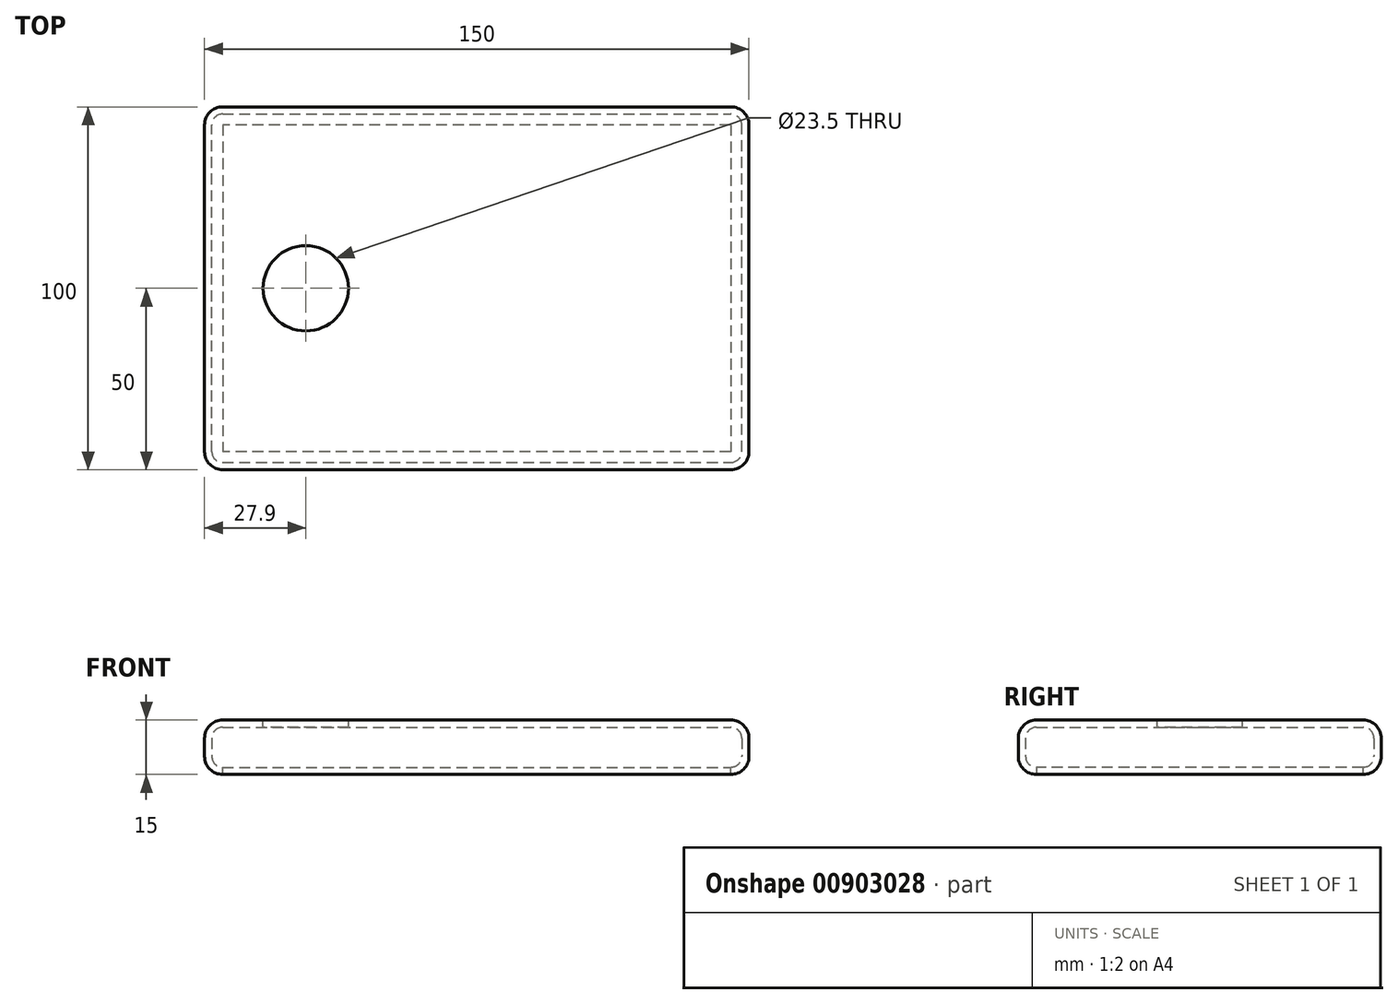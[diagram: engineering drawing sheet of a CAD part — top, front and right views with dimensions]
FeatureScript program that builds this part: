
annotation { "Feature Type Name" : "Feature", "Feature Type Description" : "" }
export const myFeature = defineFeature(function(context is Context, id is Id, definition is map)
    precondition{}
    {
        {
            var Q0;
            Q0=qCreatedBy(makeId("Top.planeOp"),FACE);
            var sketch = newSketch(context, id + "F0", { "sketchPlane" : qUnion([Q0])});
            skLineSegment(sketch, "E0.bottom", {"start": v(75, 50) * mm, "end": v(-75, 50) * mm});
            skLineSegment(sketch, "E0.top", {"start": v(75, -50) * mm, "end": v(-75, -50) * mm});
            skLineSegment(sketch, "E0.left", {"start": v(75, 50) * mm, "end": v(75, -50) * mm});
            skLineSegment(sketch, "E0.right", {"start": v(-75, 50) * mm, "end": v(-75, -50) * mm});
            skPoint(sketch, "E0.middle", {"position": v(0, 0) * mm});
            skSolve(sketch);
        }
        {
            var Q0;
            Q0=makeQuery(id+"F0.imprint","IMPRINT",FACE,{"disambiguationData":[TD([[makeQuery(id+"F0.imprint","IMPRINT",EDGE,{"derivedFrom":sQuery(id+"F0.wireOp",EDGE,"E0.bottom")}),1.0]])]});
            extrude(context, id + "F1", {"entities" : qUnion([Q0]), "depth" : 15 * mm, "offsetDistance" : 25 * mm});
        }
        {
            var Q0;
            Q0=makeQuery(id+"F1.opExtrude","CAP_EDGE",EDGE,{"disambiguationData":[OSD([sQuery(id+"F0.wireOp",EDGE,"E0.bottom")])],"isStart":true});
            var Q1;
            Q1=makeQuery(id+"F1.opExtrude","CAP_FACE",FACE,{"disambiguationData":[OSD([sQuery(id+"F0.wireOp",EDGE,"E0.bottom"),sQuery(id+"F0.wireOp",EDGE,"E0.top"),sQuery(id+"F0.wireOp",EDGE,"E0.left"),sQuery(id+"F0.wireOp",EDGE,"E0.right")])],"isStart":false});
            var Q2;
            Q2=makeQuery(id+"F1.opExtrude","SWEPT_FACE",FACE,{"disambiguationData":[OSD([sQuery(id+"F0.wireOp",EDGE,"E0.right")])]});
            var Q3;
            Q3=makeQuery(id+"F1.opExtrude","SWEPT_FACE",FACE,{"disambiguationData":[OSD([sQuery(id+"F0.wireOp",EDGE,"E0.top")])]});
            var Q4;
            Q4=makeQuery(id+"F1.opExtrude","SWEPT_FACE",FACE,{"disambiguationData":[OSD([sQuery(id+"F0.wireOp",EDGE,"E0.left")])]});
            fillet(context, id + "F2", {"entities" : qUnion([Q0, Q1, Q2, Q3, Q4]), "radius" : 5 * mm, "tangentPropagation" : true, "allowEdgeOverflow" : false});
        }
        {
            var Q0;
            Q0=makeQuery(id+"F1.opExtrude","CAP_FACE",FACE,{"disambiguationData":[OSD([sQuery(id+"F0.wireOp",EDGE,"E0.bottom"),sQuery(id+"F0.wireOp",EDGE,"E0.top"),sQuery(id+"F0.wireOp",EDGE,"E0.left"),sQuery(id+"F0.wireOp",EDGE,"E0.right")])],"isStart":true});
            shell(context, id + "F3", {"entities" : qUnion([Q0]), "thickness" : 2 * mm});
        }
        {
            var Q0;
            Q0=makeQuery(id+"F1.opExtrude","CAP_FACE",FACE,{"disambiguationData":[OSD([sQuery(id+"F0.wireOp",EDGE,"E0.bottom"),sQuery(id+"F0.wireOp",EDGE,"E0.top"),sQuery(id+"F0.wireOp",EDGE,"E0.left"),sQuery(id+"F0.wireOp",EDGE,"E0.right")])],"isStart":false});
            var sketch = newSketch(context, id + "F4", { "sketchPlane" : qUnion([Q0])});
            skCircle(sketch, "E1", {"center": v(-47.1, 0) * mm, "radius": 11.75 * mm});
            skSolve(sketch);
        }
        {
            var Q0;
            Q0 = qSketchRegion(id + "F4", true);
            extrude(context, id + "F5", {"entities" : qUnion([Q0]), "operationType" : NewBodyOperationType.REMOVE, "oppositeDirection" : true, "depth" : 25 * mm, "offsetDistance" : 25 * mm});
        }
    });
